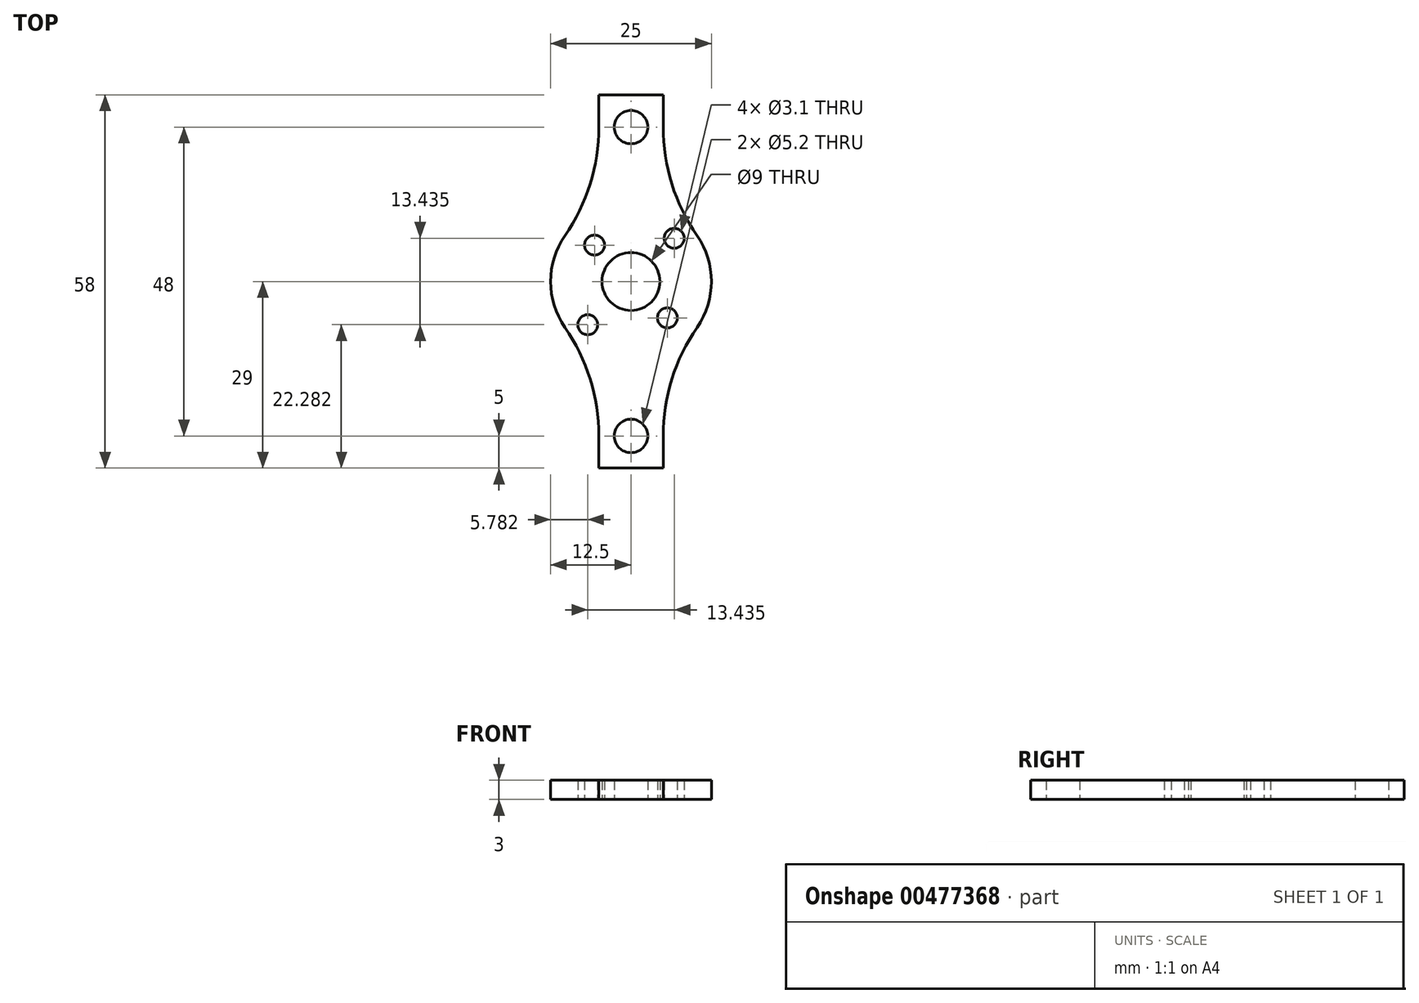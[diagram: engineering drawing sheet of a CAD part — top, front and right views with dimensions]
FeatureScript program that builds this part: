
annotation { "Feature Type Name" : "Feature", "Feature Type Description" : "" }
export const myFeature = defineFeature(function(context is Context, id is Id, definition is map)
    precondition{}
    {
        {
            var Q0;
            Q0=qCreatedBy(makeId("Top.planeOp"),FACE);
            var sketch = newSketch(context, id + "F0", { "sketchPlane" : qUnion([Q0])});
            skCircle(sketch, "E0", {"center": v(0, 0) * mm, "radius": 9.5 * mm, "construction": true});
            skCircle(sketch, "E1", {"center": v(-6.72, -6.72) * mm, "radius": 1.55 * mm});
            skLineSegment(sketch, "E2", {"start": v(-12.5, 0) * mm, "end": v(12.5, 0) * mm, "construction": true});
            skLineSegment(sketch, "E3", {"start": v(0, 29) * mm, "end": v(0, -29) * mm, "construction": true});
            skCircle(sketch, "E4", {"center": v(0, 24) * mm, "radius": 2.6 * mm});
            skCircle(sketch, "E5.MirrorC", {"center": v(0, -24) * mm, "radius": 2.6 * mm});
            skLineSegment(sketch, "E6", {"start": v(-6.72, -6.72) * mm, "end": v(0, 0) * mm, "construction": true});
            skLineSegment(sketch, "E7", {"start": v(0, 0) * mm, "end": v(6.72, -6.72) * mm, "construction": true});
            skCircle(sketch, "E8.MirrorC", {"center": v(6.72, 6.72) * mm, "radius": 1.55 * mm});
            skCircle(sketch, "E9", {"center": v(0, 0) * mm, "radius": 8 * mm, "construction": true});
            skCircle(sketch, "E10", {"center": v(5.66, -5.66) * mm, "radius": 1.55 * mm});
            skCircle(sketch, "E11.MirrorC", {"center": v(-5.66, 5.66) * mm, "radius": 1.55 * mm});
            skArc(sketch, "E12", {"start": v(-10.28, 7.12) * mm, "mid": v(-11.93, 3.73) * mm, "end": v(-12.5, 0) * mm});
            skArc(sketch, "E13", {"start": v(-10.28, 7.12) * mm, "mid": v(-6.35, 15.16) * mm, "end": v(-5, 24) * mm});
            skArc(sketch, "E14.MirrorCS", {"start": v(-10.28, -7.12) * mm, "mid": v(-11.93, -3.73) * mm, "end": v(-12.5, 0) * mm});
            skArc(sketch, "E15.MirrorCS", {"start": v(-10.28, -7.12) * mm, "mid": v(-6.35, -15.16) * mm, "end": v(-5, -24) * mm});
            skArc(sketch, "E16.MirrorCS", {"start": v(10.28, 7.12) * mm, "mid": v(6.35, 15.16) * mm, "end": v(5, 24) * mm});
            skArc(sketch, "E17.MirrorCS", {"start": v(10.28, 7.12) * mm, "mid": v(11.93, 3.73) * mm, "end": v(12.5, 0) * mm});
            skArc(sketch, "E18.MirrorCS", {"start": v(10.28, -7.12) * mm, "mid": v(11.93, -3.73) * mm, "end": v(12.5, 0) * mm});
            skArc(sketch, "E19.MirrorCS", {"start": v(10.28, -7.12) * mm, "mid": v(6.35, -15.16) * mm, "end": v(5, -24) * mm});
            skCircle(sketch, "E20", {"center": v(0, 0) * mm, "radius": 4.5 * mm});
            skLineSegment(sketch, "E21", {"start": v(-5, 24) * mm, "end": v(-5, 29) * mm});
            skLineSegment(sketch, "E22", {"start": v(-5, 29) * mm, "end": v(5, 29) * mm});
            skLineSegment(sketch, "E23", {"start": v(5, 29) * mm, "end": v(5, 24) * mm});
            skLineSegment(sketch, "E24.MirrorCS", {"start": v(-5, -24) * mm, "end": v(-5, -29) * mm});
            skLineSegment(sketch, "E25.MirrorCS", {"start": v(-5, -29) * mm, "end": v(5, -29) * mm});
            skLineSegment(sketch, "E26.MirrorCS", {"start": v(5, -29) * mm, "end": v(5, -24) * mm});
            skPoint(sketch, "E27.MirrorCS.start.orphan", {"position": v(0, 29) * mm});
            skPoint(sketch, "E28.MirrorCS.end.orphan", {"position": v(-5, -24) * mm});
            skPoint(sketch, "E29.MirrorCS.end.orphan", {"position": v(5, -24) * mm});
            skPoint(sketch, "E29.MirrorCS.start.orphan", {"position": v(0, -29) * mm});
            skPoint(sketch, "E30.MirrorCS.end.orphan", {"position": v(5, 24) * mm});
            skPoint(sketch, "E30.MirrorCS.start.orphan", {"position": v(5, 24) * mm});
            skSolve(sketch);
        }
        {
            var Q0;
            Q0=makeQuery(id+"F0.imprint","IMPRINT",FACE,{"disambiguationData":[TD([[makeQuery(id+"F0.imprint","IMPRINT",EDGE,{"derivedFrom":sQuery(id+"F0.wireOp",EDGE,"E1")}),-1.0]])]});
            extrude(context, id + "F1", {"entities" : qUnion([Q0]), "depth" : 3 * mm});
        }
    });
